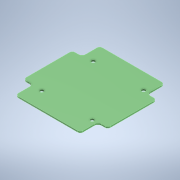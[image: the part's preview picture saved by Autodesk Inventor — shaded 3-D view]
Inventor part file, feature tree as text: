
AUTODESK INVENTOR PART (.ipt)
format: ipt  version: 2021 (Build 250183000, 183)  size: 162,304 bytes
history: native  units: mm
features: sketch x3, extrude x2, fillet x2, hole x1
ambient origin geometry x8: Origin, YZ Plane, XZ Plane, XY Plane, X Axis, Y Axis, Z Axis, Center Point
bodies: Solid1 (feature_tree)
feature tree (8):
  extrude  "Extrusion1"  Depth=95.0mm
  extrude  "Extrusion2"  Depth=11.0mm
  fillet  "Fillet1"  Radius=20.0mm
  fillet  "Fillet2"  Radius=20.0mm
  hole  "Hole2"  [1 undecoded]
  sketch  "Sketch1"  dims[d0=95.0mm d1=95.0mm]
  sketch  "Sketch4"  dims[d2=1.6mm d3=0.0mm d18=11.0mm d19=20.0mm d21=20.0mm]
  sketch  "Sketch6"  dims[d22=11.0mm d23=11.0mm d24=20.0mm d25=11.0mm d26=20.0mm d27=1.6mm d28=0.0mm d29=4.0mm d30=3.0mm d31=57.0mm d32=58.0mm d33=4.2mm d34=6.0mm d35=4.0mm d36=2.0mm d37=90.0deg d38=8.0mm d39=20.594885mm d41=3.0mm]
note: 1 required parameter value undecoded (feature->parameter linkage not recoverable at this tier; creation-order binding heuristic only, values carry confidence <= 0.55)
